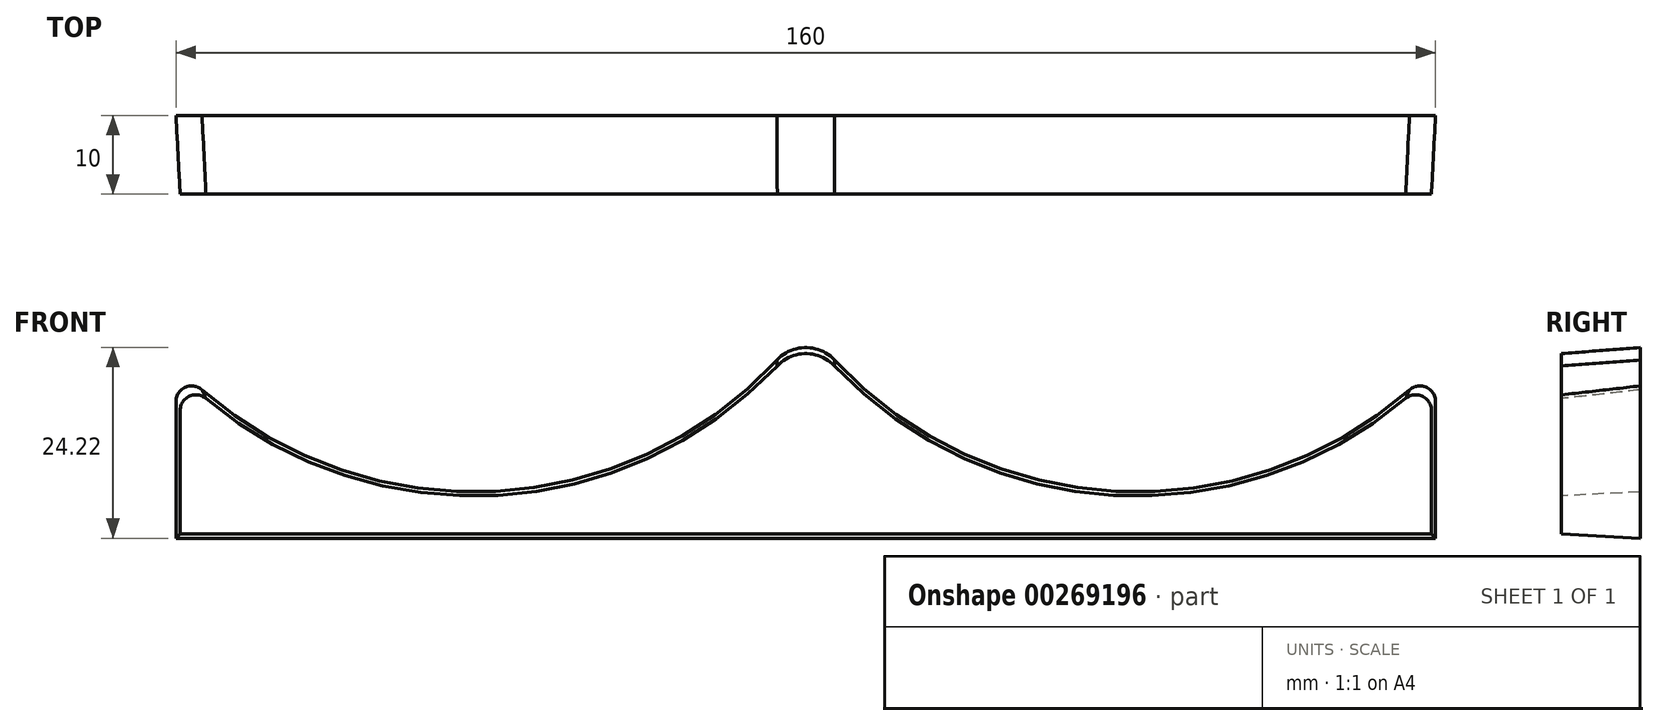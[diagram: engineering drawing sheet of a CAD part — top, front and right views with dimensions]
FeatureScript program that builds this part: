
annotation { "Feature Type Name" : "Feature", "Feature Type Description" : "" }
export const myFeature = defineFeature(function(context is Context, id is Id, definition is map)
    precondition{}
    {
        {
            var Q0;
            Q0=qCreatedBy(makeId("Front.planeOp"),FACE);
            var sketch = newSketch(context, id + "F0", { "sketchPlane" : qUnion([Q0])});
            skLineSegment(sketch, "E0", {"start": v(80, 22) * mm, "end": v(80, 0) * mm});
            skLineSegment(sketch, "E1", {"start": v(80, 0) * mm, "end": v(0, 0) * mm});
            skLineSegment(sketch, "E2", {"start": v(0, 0) * mm, "end": v(-80, 0) * mm});
            skLineSegment(sketch, "E3", {"start": v(-80, 0) * mm, "end": v(-80, 22) * mm});
            skLineSegment(sketch, "E4", {"start": v(-80, 22) * mm, "end": v(80, 22) * mm});
            skArc(sketch, "E5", {"start": v(-80, 22) * mm, "mid": v(-38.84, 6) * mm, "end": v(0, 27) * mm});
            skPoint(sketch, "E6", {"position": v(-38.84, 6) * mm});
            skPoint(sketch, "E7", {"position": v(38.84, 6) * mm});
            skArc(sketch, "E8", {"start": v(0, 27) * mm, "mid": v(38.84, 6) * mm, "end": v(80, 22) * mm});
            skSolve(sketch);
        }
        {
            var Q0;
            Q0=makeQuery(id+"F0.imprint","IMPRINT",FACE,{"disambiguationData":[TD([[makeQuery(id+"F0.imprint","IMPRINT",EDGE,{"derivedFrom":sQuery(id+"F0.wireOp",EDGE,"E0")}),-1.0]])]});
            var Q1;
            {var subQ0=sQuery(id+"F0.wireOp",EDGE,"E8");var subQ1=sQuery(id+"F0.wireOp",EDGE,"E4");var subQ2=makeQuery(id+"F0.imprint","INTERSECT",VERTEX,{"derivedFrom":[subQ1,subQ0]});Q1=makeQuery(id+"F0.imprint","IMPRINT",FACE,{"disambiguationData":[TD([[makeQuery(id+"F0.imprint","IMPRINT",EDGE,{"disambiguationData":[TD([[subQ2,1.0]])],"derivedFrom":subQ1}),1.0]])]});}
            extrude(context, id + "F1", {"entities" : qUnion([Q0, Q1]), "depth" : 10 * mm, "offsetDistance" : 25 * mm, "hasDraft" : true, "draftAngle" : 3 * degree, "draftPullDirection" : true});
        }
        {
            var Q0;
            Q0=makeQuery(id+"F1.opExtrude","SWEPT_EDGE",EDGE,{"disambiguationData":[OSD([sQuery(id+"F0.wireOp",EDGE,"E4"),sQuery(id+"F0.wireOp",EDGE,"E5"),sQuery(id+"F0.wireOp",EDGE,"E8")])]});
            fillet(context, id + "F2", {"entities" : qUnion([Q0]), "tangentPropagation" : true, "radius" : 5 * mm, "defaultsChanged" : true, "vertexSettings" : [], "allowEdgeOverflow" : false});
        }
        {
            var Q0;
            Q0=makeQuery(id+"F1.opExtrude","SWEPT_EDGE",EDGE,{"disambiguationData":[OSD([sQuery(id+"F0.wireOp",EDGE,"E0"),sQuery(id+"F0.wireOp",EDGE,"E4"),sQuery(id+"F0.wireOp",EDGE,"E8")])]});
            var Q1;
            Q1=makeQuery(id+"F1.opExtrude","SWEPT_EDGE",EDGE,{"disambiguationData":[OSD([sQuery(id+"F0.wireOp",EDGE,"E3"),sQuery(id+"F0.wireOp",EDGE,"E4"),sQuery(id+"F0.wireOp",EDGE,"E5")])]});
            fillet(context, id + "F3", {"entities" : qUnion([Q0, Q1]), "tangentPropagation" : true, "radius" : 2 * mm, "defaultsChanged" : false, "vertexSettings" : [], "allowEdgeOverflow" : false});
        }
    });
